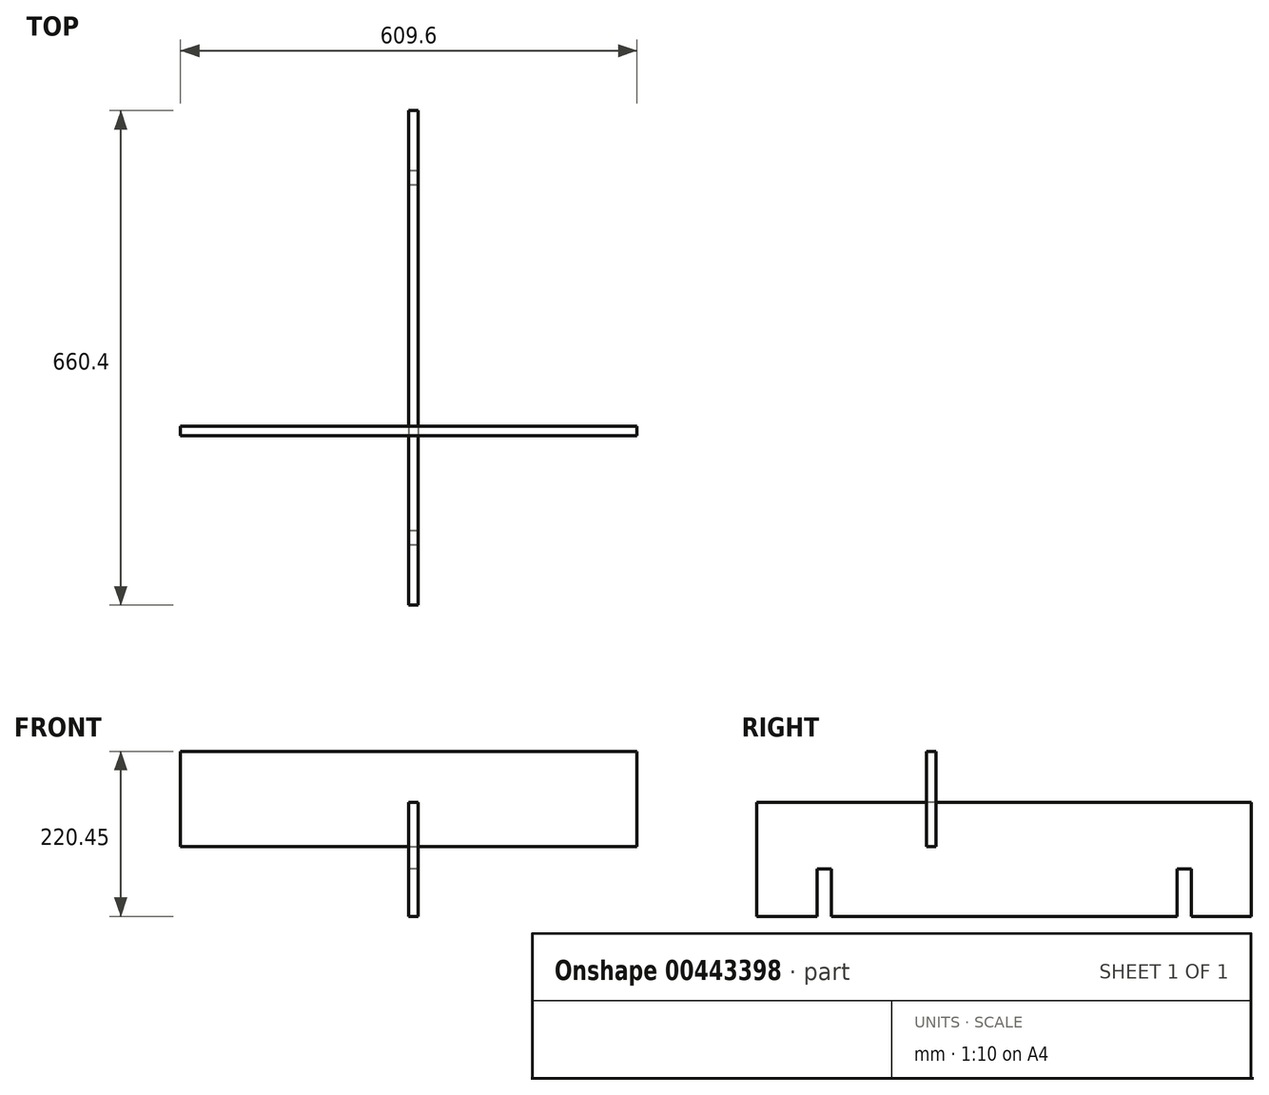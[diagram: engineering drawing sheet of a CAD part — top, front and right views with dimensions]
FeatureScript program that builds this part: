
annotation { "Feature Type Name" : "Feature", "Feature Type Description" : "" }
export const myFeature = defineFeature(function(context is Context, id is Id, definition is map)
    precondition{}
    {
        {
            var Q0;
            Q0=qCreatedBy(makeId("Front.planeOp"),FACE);
            var sketch = newSketch(context, id + "F0", { "sketchPlane" : qUnion([Q0])});
            skLineSegment(sketch, "E0.bottom", {"start": v(-304.8, 0) * mm, "end": v(304.8, 0) * mm});
            skLineSegment(sketch, "E0.top", {"start": v(-304.8, 127) * mm, "end": v(304.8, 127) * mm});
            skLineSegment(sketch, "E0.left", {"start": v(-304.8, 0) * mm, "end": v(-304.8, 127) * mm});
            skLineSegment(sketch, "E0.right", {"start": v(304.8, 0) * mm, "end": v(304.8, 127) * mm});
            skPoint(sketch, "E1", {"position": v(0, 0) * mm});
            skSolve(sketch);
        }
        {
            var Q0;
            Q0 = qSketchRegion(id + "F0", true);
            extrude(context, id + "F1", {"entities" : qUnion([Q0]), "depth" : 12.7 * mm});
        }
        {
            var Q0;
            Q0=qCreatedBy(makeId("Right.planeOp"),FACE);
            var sketch = newSketch(context, id + "F2", { "sketchPlane" : qUnion([Q0])});
            skLineSegment(sketch, "E2.bottom", {"start": v(421.15, 58.95) * mm, "end": v(-239.25, 58.95) * mm});
            skLineSegment(sketch, "E2.top", {"start": v(421.15, -93.45) * mm, "end": v(341.06, -93.45) * mm});
            skLineSegment(sketch, "E2.left", {"start": v(421.15, 58.95) * mm, "end": v(421.15, -93.45) * mm});
            skLineSegment(sketch, "E2.right", {"start": v(-239.25, 58.95) * mm, "end": v(-239.25, -93.45) * mm});
            skPoint(sketch, "E2.middle", {"position": v(90.95, -17.25) * mm});
            skLineSegment(sketch, "E3.top", {"start": v(-159.16, -29.95) * mm, "end": v(-140.11, -29.95) * mm});
            skLineSegment(sketch, "E3.left", {"start": v(-159.16, -93.45) * mm, "end": v(-159.16, -29.95) * mm});
            skLineSegment(sketch, "E3.right", {"start": v(-140.11, -93.45) * mm, "end": v(-140.11, -29.95) * mm});
            skLineSegment(sketch, "E4", {"start": v(90.95, 58.95) * mm, "end": v(90.95, -93.45) * mm, "construction": true});
            skLineSegment(sketch, "E5.MirrorCS", {"start": v(322, -93.45) * mm, "end": v(322, -29.95) * mm});
            skLineSegment(sketch, "E6.MirrorCS", {"start": v(341.06, -93.45) * mm, "end": v(341.06, -29.95) * mm});
            skLineSegment(sketch, "E7.MirrorCS", {"start": v(341.06, -29.95) * mm, "end": v(322, -29.95) * mm});
            skLineSegment(sketch, "E8.trimOffspring", {"start": v(322, -93.45) * mm, "end": v(90.95, -93.45) * mm});
            skLineSegment(sketch, "E9.trimOffspring", {"start": v(-159.16, -93.45) * mm, "end": v(-239.25, -93.45) * mm});
            skLineSegment(sketch, "E10", {"start": v(-140.11, -93.45) * mm, "end": v(90.95, -93.45) * mm});
            skSolve(sketch);
        }
        {
            var Q0;
            Q0 = qSketchRegion(id + "F2", true);
            extrude(context, id + "F3", {"entities" : qUnion([Q0]), "depth" : 12.7 * mm});
        }
    });
